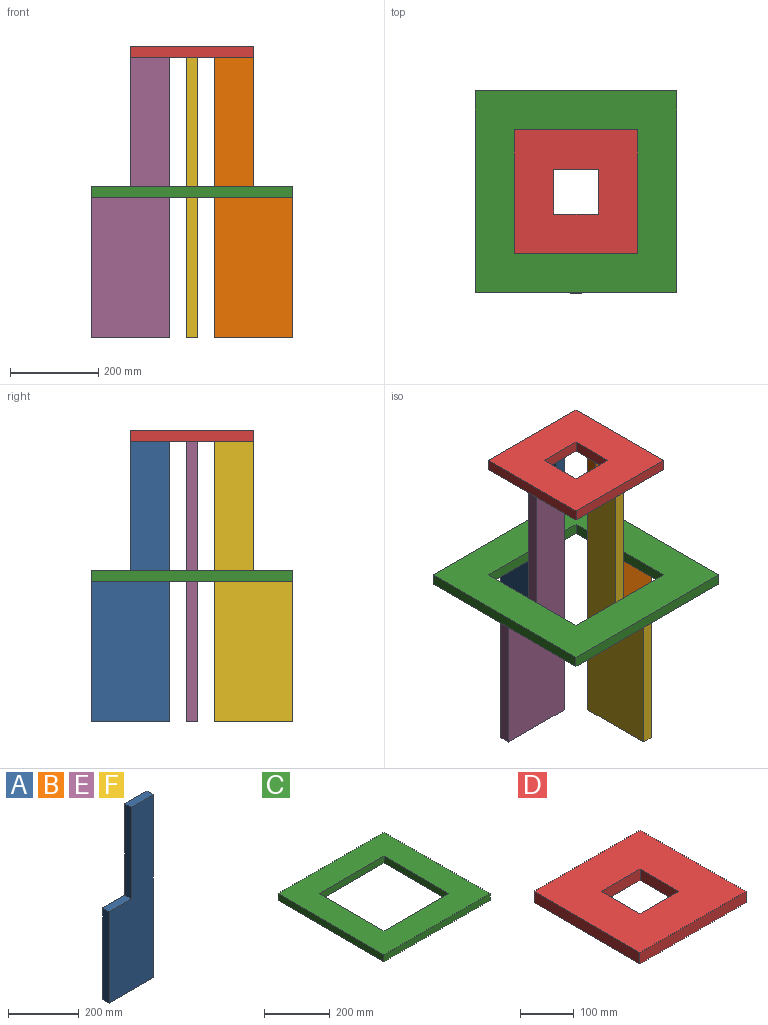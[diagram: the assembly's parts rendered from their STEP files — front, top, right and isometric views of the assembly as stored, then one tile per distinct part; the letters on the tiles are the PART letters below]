
ASSEMBLY  parts=6 mates=5
PART A: 8 faces, bbox 177.8x25.4x635 mm
  f0: plane 177.8x25.4mm, normal (0,0,-1), area 4516.1mm2, adj f1,f3,f4,f5
  f1: plane 635x25.4mm, normal (1,0,0), area 16129mm2, adj f0,f4,f5,f7
  f2: plane 88.9x25.4mm, normal (0,0,1), area 2258.1mm2, adj f3,f4,f5,f6
  f3: plane 317.5x25.4mm, normal (-1,0,0), area 8064.5mm2, adj f0,f2,f4,f5
  f4: plane 635x177.8mm, normal (0,-1,0), area 84677.3mm2, adj f0,f1,f2,f3,f6,f7
  f5: plane 635x177.8mm, normal (0,1,0), area 84677.3mm2, adj f0,f1,f2,f3,f6,f7
  f6: plane 317.5x25.4mm, normal (-1,0,0), area 8064.5mm2, adj f2,f4,f5,f7
  f7: plane 88.9x25.4mm, normal (0,0,1), area 2258.1mm2, adj f1,f4,f5,f6
PART B: same geometry as A
PART C: 10 faces, bbox 457.2x457.2x25.4 mm
  f0: plane 457.2x25.4mm, normal (1,0,0), area 11612.9mm2, adj f1,f7,f8,f9
  f1: plane 457.2x25.4mm, normal (0,1,0), area 11612.9mm2, adj f0,f2,f8,f9
  f2: plane 457.2x25.4mm, normal (-1,0,0), area 11612.9mm2, adj f1,f7,f8,f9
  f3: plane 279.4x25.4mm, normal (1,0,0), area 7096.8mm2, adj f4,f6,f8,f9
  f4: plane 279.4x25.4mm, normal (0,-1,0), area 7096.8mm2, adj f3,f5,f8,f9
  f5: plane 279.4x25.4mm, normal (-1,0,0), area 7096.8mm2, adj f4,f6,f8,f9
  f6: plane 279.4x25.4mm, normal (0,1,0), area 7096.8mm2, adj f3,f5,f8,f9
  f7: plane 457.2x25.4mm, normal (0,-1,0), area 11612.9mm2, adj f0,f2,f8,f9
  f8: plane 457.2x457.2mm, normal (0,0,1), area 130967.5mm2, adj f0,f1,f2,f3,f4,f5,f6,f7
  f9: plane 457.2x457.2mm, normal (0,0,-1), area 130967.5mm2, adj f0,f1,f2,f3,f4,f5,f6,f7
PART D: 10 faces, bbox 279.4x279.4x25.4 mm
  f0: plane 279.4x25.4mm, normal (0,1,0), area 7096.8mm2, adj f1,f7,f8,f9
  f1: plane 279.4x25.4mm, normal (-1,0,0), area 7096.8mm2, adj f0,f2,f8,f9
  f2: plane 279.4x25.4mm, normal (0,-1,0), area 7096.8mm2, adj f1,f7,f8,f9
  f3: plane 101.6x25.4mm, normal (1,0,0), area 2580.6mm2, adj f4,f6,f8,f9
  f4: plane 101.6x25.4mm, normal (0,-1,0), area 2580.6mm2, adj f3,f5,f8,f9
  f5: plane 101.6x25.4mm, normal (-1,0,0), area 2580.6mm2, adj f4,f6,f8,f9
  f6: plane 101.6x25.4mm, normal (0,1,0), area 2580.6mm2, adj f3,f5,f8,f9
  f7: plane 279.4x25.4mm, normal (1,0,0), area 7096.8mm2, adj f0,f2,f8,f9
  f8: plane 279.4x279.4mm, normal (0,0,1), area 67741.8mm2, adj f0,f1,f2,f3,f4,f5,f6,f7
  f9: plane 279.4x279.4mm, normal (0,0,-1), area 67741.8mm2, adj f0,f1,f2,f3,f4,f5,f6,f7
PART E: same geometry as A
PART F: same geometry as A
PLACE A rot(axis=(0,0,-1),90deg) t=(-224.06,-1194.15,137)mm
PLACE B rot(axis=(0,0,1),180deg) t=(-185.96,-1257.65,137)mm
PLACE C t=(-236.76,-1244.95,454.5)mm
PLACE D t=(-186.73,-1291.04,772)mm
PLACE E t=(-287.56,-1232.25,137)mm
PLACE F rot(axis=(0,0,1),90deg) t=(-249.46,-1295.75,137)mm
MATE fastened C.f9 <-> E.f2  axis (0,0,-1) through (-376.46,-1244.95,454.5)mm
MATE fastened D.f9 <-> F.f7  axis (0,0,-1) through (-236.76,-1295.75,772)mm
MATE fastened E.f7 <-> D.f9  axis (0,0,1) through (-287.56,-1244.95,772)mm
MATE fastened A.f7 <-> D.f9  axis (0,0,1) through (-236.76,-1194.15,772)mm
MATE fastened B.f7 <-> D.f9  axis (0,0,1) through (-185.96,-1244.95,772)mm
